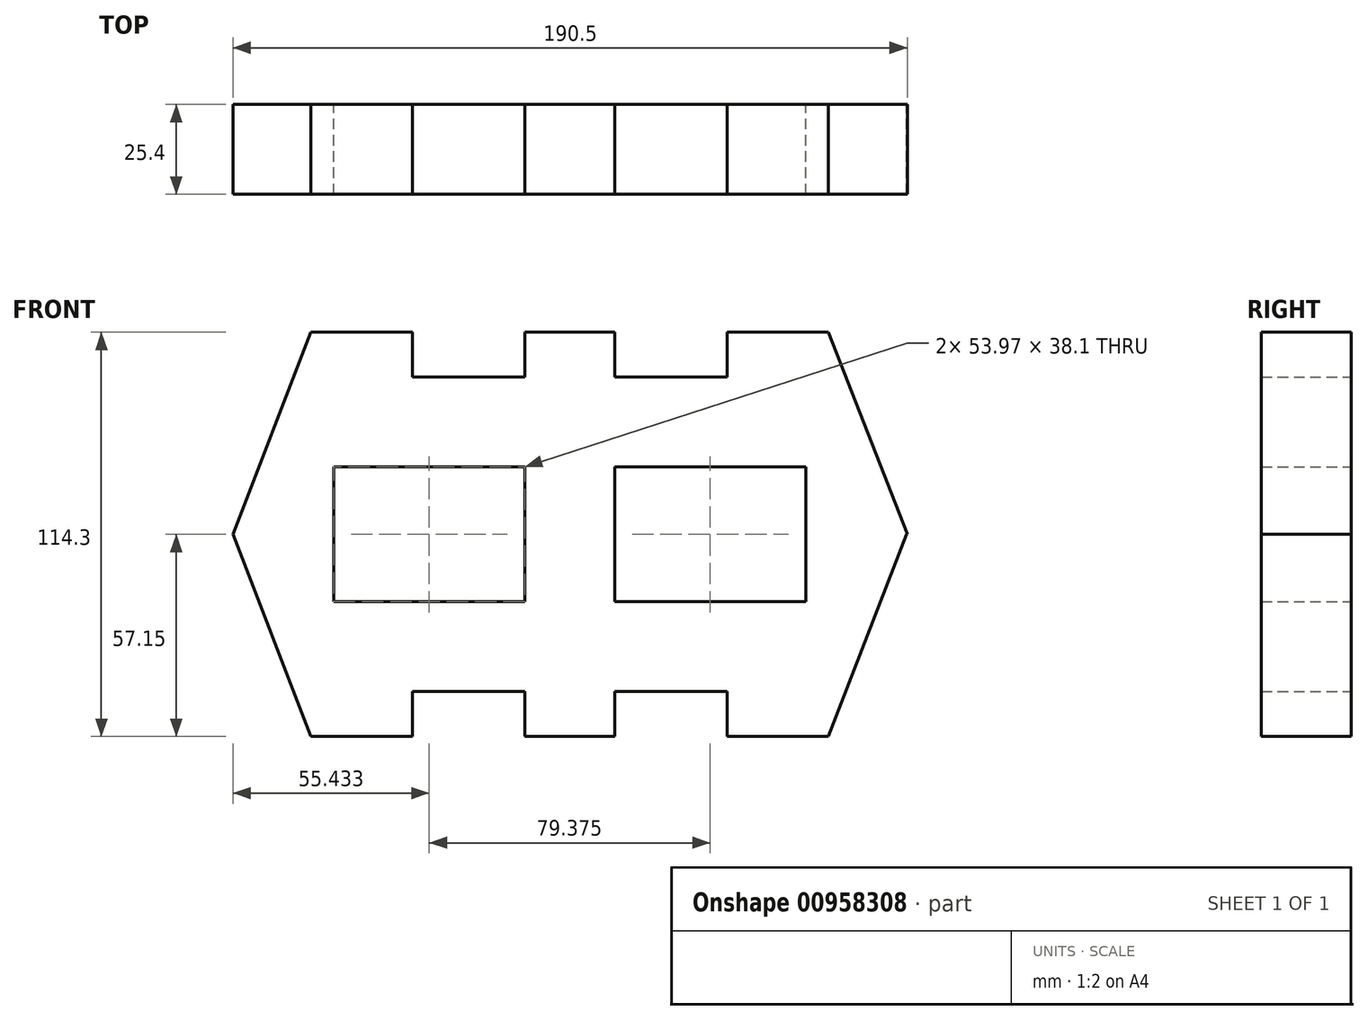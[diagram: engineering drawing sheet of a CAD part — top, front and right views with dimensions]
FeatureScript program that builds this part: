
annotation { "Feature Type Name" : "Feature", "Feature Type Description" : "" }
export const myFeature = defineFeature(function(context is Context, id is Id, definition is map)
    precondition{}
    {
        {
            var Q0;
            Q0=qCreatedBy(makeId("Front.planeOp"),FACE);
            var sketch = newSketch(context, id + "F0", { "sketchPlane" : qUnion([Q0])});
            skLineSegment(sketch, "E0.bottom", {"start": v(12.7, 57.15) * mm, "end": v(-12.7, 57.15) * mm});
            skLineSegment(sketch, "E0.top", {"start": v(12.7, -57.15) * mm, "end": v(-12.7, -57.15) * mm});
            skLineSegment(sketch, "E0.left", {"start": v(12.7, 57.15) * mm, "end": v(12.7, -57.15) * mm});
            skLineSegment(sketch, "E0.right", {"start": v(-12.7, 57.15) * mm, "end": v(-12.7, -57.15) * mm});
            skPoint(sketch, "E0.middle", {"position": v(0, 0) * mm});
            skLineSegment(sketch, "E1.bottom", {"start": v(73.1, -57.15) * mm, "end": v(44.45, -57.15) * mm});
            skLineSegment(sketch, "E1.top", {"start": v(73.1, 57.15) * mm, "end": v(44.45, 57.15) * mm});
            skLineSegment(sketch, "E2", {"start": v(73.1, 57.15) * mm, "end": v(95.38, 0) * mm});
            skLineSegment(sketch, "E3.MirrorCS", {"start": v(73.1, -57.15) * mm, "end": v(95.12, 0) * mm});
            skLineSegment(sketch, "E4.MirrorCS", {"start": v(-73.1, -57.15) * mm, "end": v(-95.12, 0) * mm});
            skLineSegment(sketch, "E5", {"start": v(12.7, 57.15) * mm, "end": v(12.7, 44.45) * mm});
            skLineSegment(sketch, "E6", {"start": v(12.7, 44.45) * mm, "end": v(44.45, 44.45) * mm});
            skLineSegment(sketch, "E7", {"start": v(44.45, 44.45) * mm, "end": v(44.45, 57.15) * mm});
            skLineSegment(sketch, "E8.MirrorCS", {"start": v(44.45, -44.45) * mm, "end": v(44.45, -57.15) * mm});
            skLineSegment(sketch, "E9.MirrorCS", {"start": v(12.7, -44.45) * mm, "end": v(44.45, -44.45) * mm});
            skLineSegment(sketch, "E10.MirrorCS", {"start": v(-12.7, 44.45) * mm, "end": v(-44.45, 44.45) * mm});
            skLineSegment(sketch, "E11.MirrorCS", {"start": v(-44.45, 44.45) * mm, "end": v(-44.45, 57.15) * mm});
            skLineSegment(sketch, "E12.MirrorCS", {"start": v(-12.7, -44.45) * mm, "end": v(-44.45, -44.45) * mm});
            skLineSegment(sketch, "E13.MirrorCS", {"start": v(-44.45, -44.45) * mm, "end": v(-44.45, -57.15) * mm});
            skLineSegment(sketch, "E14.trimOffspring", {"start": v(-44.45, 57.15) * mm, "end": v(-73.1, 57.15) * mm});
            skLineSegment(sketch, "E15.trimOffspring", {"start": v(-44.45, -57.15) * mm, "end": v(-73.1, -57.15) * mm});
            skLineSegment(sketch, "E16", {"start": v(-73.1, 57.15) * mm, "end": v(-95.12, 0) * mm});
            skPoint(sketch, "E17", {"position": v(-12.7, 19.05) * mm});
            skPoint(sketch, "E18", {"position": v(-66.68, 0) * mm});
            skPoint(sketch, "E19", {"position": v(-12.7, 0) * mm});
            skLineSegment(sketch, "E20.bottom", {"start": v(-12.7, 19.05) * mm, "end": v(-66.68, 19.05) * mm});
            skLineSegment(sketch, "E20.left", {"start": v(-12.7, 19.05) * mm, "end": v(-12.7, 0) * mm});
            skLineSegment(sketch, "E20.right", {"start": v(-66.68, 19.05) * mm, "end": v(-66.68, 0) * mm});
            skLineSegment(sketch, "E21.MirrorCS", {"start": v(-66.68, -19.05) * mm, "end": v(-66.68, 0) * mm});
            skLineSegment(sketch, "E22.MirrorCS", {"start": v(-12.7, -19.05) * mm, "end": v(-66.68, -19.05) * mm});
            skLineSegment(sketch, "E23.MirrorCS", {"start": v(12.7, 19.05) * mm, "end": v(66.68, 19.05) * mm});
            skLineSegment(sketch, "E24.MirrorCS", {"start": v(66.68, 19.05) * mm, "end": v(66.68, 0) * mm});
            skLineSegment(sketch, "E25.MirrorCS", {"start": v(66.68, -19.05) * mm, "end": v(66.68, 0) * mm});
            skLineSegment(sketch, "E26.MirrorCS", {"start": v(12.7, -19.05) * mm, "end": v(66.68, -19.05) * mm});
            skLineSegment(sketch, "E27.trimOffspring", {"start": v(-12.7, 0) * mm, "end": v(12.7, 0) * mm});
            skLineSegment(sketch, "E28.trimOffspring", {"start": v(95.12, 0) * mm, "end": v(95.38, 0) * mm});
            skSolve(sketch);
        }
        {
            var Q0;
            Q0=makeQuery(id+"F0.imprint","IMPRINT",FACE,{"disambiguationData":[TD([[makeQuery(id+"F0.imprint","IMPRINT",EDGE,{"derivedFrom":sQuery(id+"F0.wireOp",EDGE,"E4.MirrorCS")}),-1.0]])]});
            var Q1;
            {var subQ1=sQuery(id+"F0.wireOp",EDGE,"E0.bottom");Q1=makeQuery(id+"F0.imprint","IMPRINT",FACE,{"disambiguationData":[TD([[makeQuery(id+"F0.imprint","IMPRINT",EDGE,{"derivedFrom":subQ1}),1.0]])]});}
            var Q2;
            {var subQ4=sQuery(id+"F0.wireOp",EDGE,"E0.top");Q2=makeQuery(id+"F0.imprint","IMPRINT",FACE,{"disambiguationData":[TD([[makeQuery(id+"F0.imprint","IMPRINT",EDGE,{"derivedFrom":subQ4}),-1.0]])]});}
            var Q3;
            Q3=makeQuery(id+"F0.imprint","IMPRINT",FACE,{"disambiguationData":[TD([[makeQuery(id+"F0.imprint","IMPRINT",EDGE,{"derivedFrom":sQuery(id+"F0.wireOp",EDGE,"E1.bottom")}),-1.0]])]});
            extrude(context, id + "F1", {"entities" : qUnion([Q0, Q1, Q2, Q3]), "depth" : 25.4 * mm, "offsetDistance" : 25.4 * mm});
        }
    });
